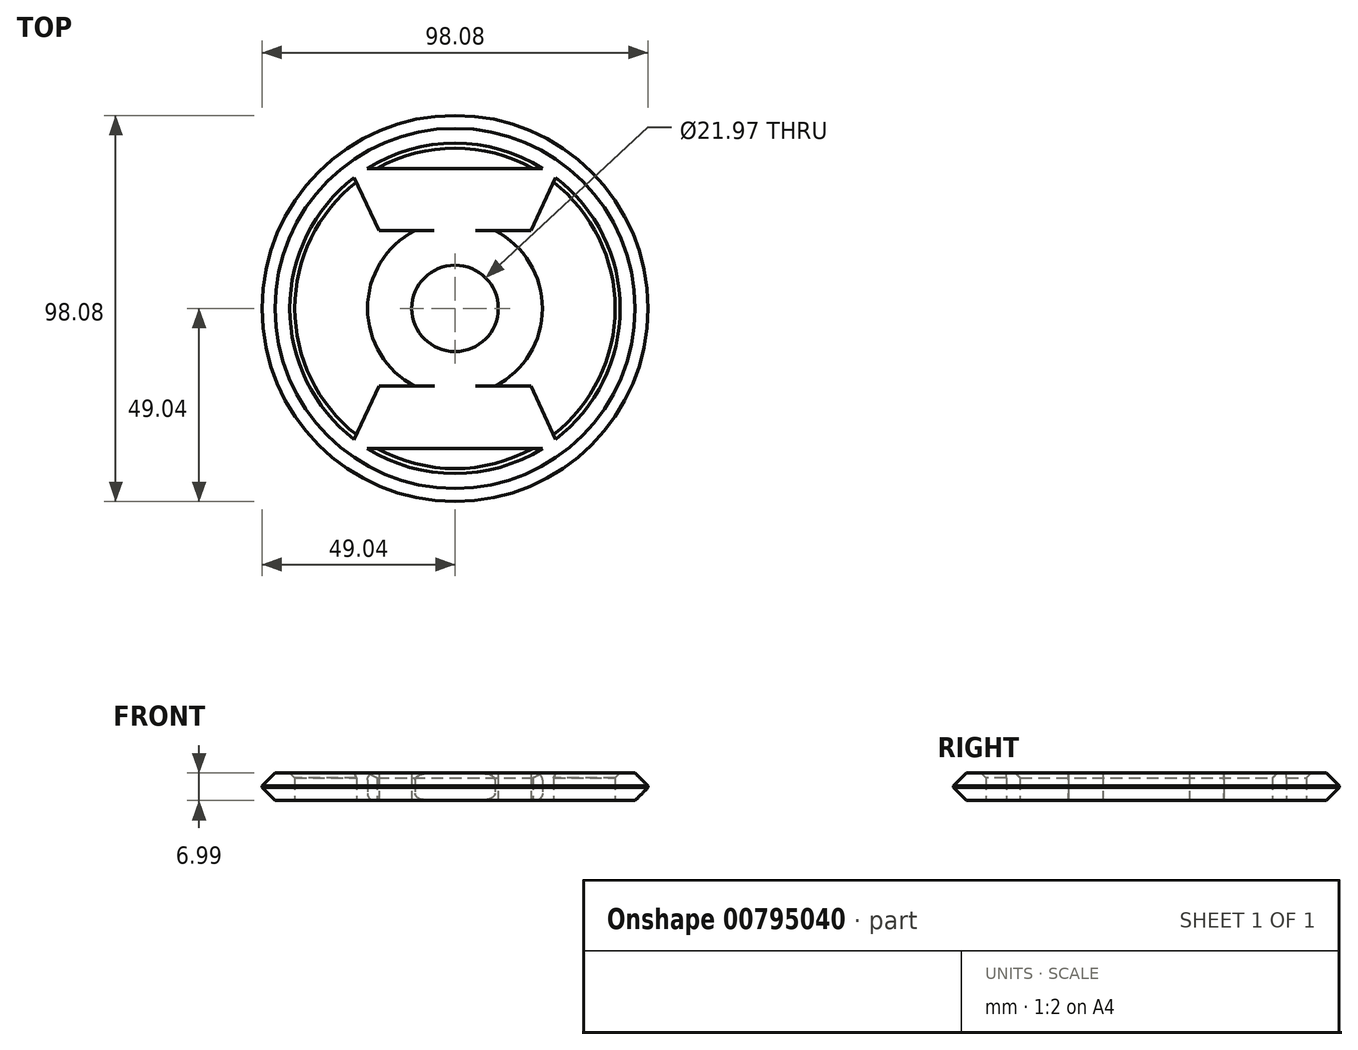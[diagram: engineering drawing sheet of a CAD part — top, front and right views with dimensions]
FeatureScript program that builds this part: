
annotation { "Feature Type Name" : "Feature", "Feature Type Description" : "" }
export const myFeature = defineFeature(function(context is Context, id is Id, definition is map)
    precondition{}
    {
        {
            var Q0;
            Q0=qCreatedBy(makeId("Top.planeOp"),FACE);
            var sketch = newSketch(context, id + "F0", { "sketchPlane" : qUnion([Q0])});
            skCircle(sketch, "E0", {"center": v(0, 0) * mm, "radius": 10.99 * mm});
            skCircle(sketch, "E1", {"center": v(0, 0) * mm, "radius": 22.23 * mm});
            skPoint(sketch, "E2", {"position": v(0, 35.56) * mm});
            skPoint(sketch, "E3", {"position": v(0, -35.56) * mm});
            skPoint(sketch, "E4", {"position": v(-26.67, 35.56) * mm});
            skPoint(sketch, "E5", {"position": v(26.67, 35.56) * mm});
            skPoint(sketch, "E6", {"position": v(-26.67, -35.56) * mm});
            skPoint(sketch, "E7", {"position": v(26.67, -35.56) * mm});
            skLineSegment(sketch, "E8", {"start": v(-26.67, 35.56) * mm, "end": v(26.67, 35.56) * mm});
            skLineSegment(sketch, "E9", {"start": v(-26.67, -35.56) * mm, "end": v(26.67, -35.56) * mm});
            skPoint(sketch, "E10", {"position": v(0, 19.75) * mm});
            skLineSegment(sketch, "E11", {"start": v(-26.67, 35.56) * mm, "end": v(-19.3, 19.75) * mm});
            skLineSegment(sketch, "E12", {"start": v(0, 19.75) * mm, "end": v(-19.3, 19.75) * mm});
            skLineSegment(sketch, "E13", {"start": v(0, 19.75) * mm, "end": v(19.3, 19.75) * mm});
            skLineSegment(sketch, "E14", {"start": v(26.67, 35.56) * mm, "end": v(19.3, 19.75) * mm});
            skPoint(sketch, "E15", {"position": v(0, -19.76) * mm});
            skLineSegment(sketch, "E16", {"start": v(0, -19.76) * mm, "end": v(-19.3, -19.76) * mm});
            skLineSegment(sketch, "E17", {"start": v(-19.3, -19.76) * mm, "end": v(-26.67, -35.56) * mm});
            skLineSegment(sketch, "E18", {"start": v(0, -19.76) * mm, "end": v(19.3, -19.76) * mm});
            skLineSegment(sketch, "E19", {"start": v(19.3, -19.76) * mm, "end": v(26.67, -35.56) * mm});
            skCircle(sketch, "E20", {"center": v(0, 0) * mm, "radius": 40.7 * mm});
            skCircle(sketch, "E21", {"center": v(0, 0) * mm, "radius": 49.04 * mm});
            skSolve(sketch);
        }
        {
            var Q0;
            Q0=makeQuery(id+"F0.imprint","IMPRINT",FACE,{"disambiguationData":[TD([[makeQuery(id+"F0.imprint","IMPRINT",EDGE,{"derivedFrom":sQuery(id+"F0.wireOp",EDGE,"E21")}),1.0]])]});
            var Q1;
            {var subQ0=sQuery(id+"F0.wireOp",EDGE,"E12");var subQ3=sQuery(id+"F0.wireOp",EDGE,"E1");var subQ4=makeQuery(id+"F0.imprint","INTERSECT",VERTEX,{"derivedFrom":[subQ3,subQ0]});Q1=makeQuery(id+"F0.imprint","IMPRINT",FACE,{"disambiguationData":[TD([[makeQuery(id+"F0.imprint","IMPRINT",EDGE,{"disambiguationData":[TD([[subQ4,1.0]])],"derivedFrom":subQ3}),-1.0]])]});}
            var Q2;
            {var subQ0=sQuery(id+"F0.wireOp",EDGE,"E11");var subQ1=sQuery(id+"F0.wireOp",EDGE,"E8");var subQ2=makeQuery(id+"F0.imprint","INTERSECT",VERTEX,{"derivedFrom":[subQ1,subQ0]});Q2=makeQuery(id+"F0.imprint","IMPRINT",FACE,{"disambiguationData":[TD([[makeQuery(id+"F0.imprint","IMPRINT",EDGE,{"disambiguationData":[TD([[subQ2,-1.0]])],"derivedFrom":subQ1}),-1.0]])]});}
            var Q3;
            {var subQ0=sQuery(id+"F0.wireOp",EDGE,"E14");var subQ1=sQuery(id+"F0.wireOp",EDGE,"E8");var subQ2=makeQuery(id+"F0.imprint","INTERSECT",VERTEX,{"derivedFrom":[subQ1,subQ0]});Q3=makeQuery(id+"F0.imprint","IMPRINT",FACE,{"disambiguationData":[TD([[makeQuery(id+"F0.imprint","IMPRINT",EDGE,{"disambiguationData":[TD([[subQ2,1.0]])],"derivedFrom":subQ1}),-1.0]])]});}
            var Q4;
            Q4=makeQuery(id+"F0.imprint","IMPRINT",FACE,{"disambiguationData":[TD([[makeQuery(id+"F0.imprint","IMPRINT",EDGE,{"derivedFrom":sQuery(id+"F0.wireOp",EDGE,"E0")}),-1.0]])]});
            var Q5;
            {var subQ0=sQuery(id+"F0.wireOp",EDGE,"E12");var subQ1=sQuery(id+"F0.wireOp",EDGE,"E1");var subQ2=makeQuery(id+"F0.imprint","INTERSECT",VERTEX,{"derivedFrom":[subQ1,subQ0]});Q5=makeQuery(id+"F0.imprint","IMPRINT",FACE,{"disambiguationData":[TD([[makeQuery(id+"F0.imprint","IMPRINT",EDGE,{"disambiguationData":[TD([[subQ2,1.0]])],"derivedFrom":subQ1}),1.0]])]});}
            var Q6;
            {var subQ1=sQuery(id+"F0.wireOp",EDGE,"E16");var subQ5=sQuery(id+"F0.wireOp",EDGE,"E1");var subQ6=makeQuery(id+"F0.imprint","INTERSECT",VERTEX,{"derivedFrom":[subQ5,subQ1]});Q6=makeQuery(id+"F0.imprint","IMPRINT",FACE,{"disambiguationData":[TD([[makeQuery(id+"F0.imprint","IMPRINT",EDGE,{"disambiguationData":[TD([[subQ6,-1.0]])],"derivedFrom":subQ5}),-1.0]])]});}
            var Q7;
            {var subQ0=sQuery(id+"F0.wireOp",EDGE,"E16");var subQ1=sQuery(id+"F0.wireOp",EDGE,"E1");var subQ2=makeQuery(id+"F0.imprint","INTERSECT",VERTEX,{"derivedFrom":[subQ1,subQ0]});Q7=makeQuery(id+"F0.imprint","IMPRINT",FACE,{"disambiguationData":[TD([[makeQuery(id+"F0.imprint","IMPRINT",EDGE,{"disambiguationData":[TD([[subQ2,-1.0]])],"derivedFrom":subQ1}),1.0]])]});}
            var Q8;
            {var subQ0=sQuery(id+"F0.wireOp",EDGE,"E17");var subQ1=sQuery(id+"F0.wireOp",EDGE,"E9");var subQ2=makeQuery(id+"F0.imprint","INTERSECT",VERTEX,{"derivedFrom":[subQ1,subQ0]});Q8=makeQuery(id+"F0.imprint","IMPRINT",FACE,{"disambiguationData":[TD([[makeQuery(id+"F0.imprint","IMPRINT",EDGE,{"disambiguationData":[TD([[subQ2,-1.0]])],"derivedFrom":subQ1}),1.0]])]});}
            var Q9;
            {var subQ0=sQuery(id+"F0.wireOp",EDGE,"E19");var subQ1=sQuery(id+"F0.wireOp",EDGE,"E9");var subQ2=makeQuery(id+"F0.imprint","INTERSECT",VERTEX,{"derivedFrom":[subQ1,subQ0]});Q9=makeQuery(id+"F0.imprint","IMPRINT",FACE,{"disambiguationData":[TD([[makeQuery(id+"F0.imprint","IMPRINT",EDGE,{"disambiguationData":[TD([[subQ2,1.0]])],"derivedFrom":subQ1}),1.0]])]});}
            extrude(context, id + "F1", {"entities" : qUnion([Q0, Q1, Q2, Q3, Q4, Q5, Q6, Q7, Q8, Q9]), "depth" : 7 * mm, "offsetDistance" : 25.4 * mm});
        }
        {
            var Q0;
            {var subQ0=sQuery(id+"F0.wireOp",EDGE,"E1");Q0=makeQuery(id+"F1.opExtrude","CAP_EDGE",EDGE,{"disambiguationData":[OSD([subQ0]),TDD([makeQuery(id+"F0.imprint","IMPRINT",EDGE,{"disambiguationData":[TD([[makeQuery(id+"F0.imprint","INTERSECT",VERTEX,{"derivedFrom":[subQ0,sQuery(id+"F0.wireOp",EDGE,"E12")]}),-1.0]])],"derivedFrom":subQ0})])],"isStart":false});}
            var Q1;
            {var subQ0=sQuery(id+"F0.wireOp",EDGE,"E1");Q1=makeQuery(id+"F1.opExtrude","CAP_EDGE",EDGE,{"disambiguationData":[OSD([subQ0]),TDD([makeQuery(id+"F0.imprint","IMPRINT",EDGE,{"disambiguationData":[TD([[makeQuery(id+"F0.imprint","INTERSECT",VERTEX,{"derivedFrom":[subQ0,sQuery(id+"F0.wireOp",EDGE,"E13")]}),1.0]])],"derivedFrom":subQ0})])],"isStart":false});}
            var Q2;
            {var subQ0=sQuery(id+"F0.wireOp",EDGE,"E1");Q2=makeQuery(id+"F1.opExtrude","CAP_EDGE",EDGE,{"disambiguationData":[OSD([subQ0]),TDD([makeQuery(id+"F0.imprint","IMPRINT",EDGE,{"disambiguationData":[TD([[makeQuery(id+"F0.imprint","INTERSECT",VERTEX,{"derivedFrom":[subQ0,sQuery(id+"F0.wireOp",EDGE,"E13")]}),1.0]])],"derivedFrom":subQ0})])],"isStart":true});}
            var Q3;
            {var subQ0=sQuery(id+"F0.wireOp",EDGE,"E1");Q3=makeQuery(id+"F1.opExtrude","CAP_EDGE",EDGE,{"disambiguationData":[OSD([subQ0]),TDD([makeQuery(id+"F0.imprint","IMPRINT",EDGE,{"disambiguationData":[TD([[makeQuery(id+"F0.imprint","INTERSECT",VERTEX,{"derivedFrom":[subQ0,sQuery(id+"F0.wireOp",EDGE,"E12")]}),-1.0]])],"derivedFrom":subQ0})])],"isStart":true});}
            fillet(context, id + "F2", {"entities" : qUnion([Q0, Q1, Q2, Q3]), "radius" : 1.78 * mm, "tangentPropagation" : true, "allowEdgeOverflow" : false});
        }
        {
            var Q0;
            {var subQ0=sQuery(id+"F0.wireOp",EDGE,"E20");Q0=makeQuery(id+"F1.opExtrude","CAP_EDGE",EDGE,{"disambiguationData":[OSD([subQ0]),TDD([makeQuery(id+"F0.imprint","IMPRINT",EDGE,{"disambiguationData":[TD([[makeQuery(id+"F0.imprint","INTERSECT",VERTEX,{"derivedFrom":[sQuery(id+"F0.wireOp",EDGE,"E11"),subQ0]}),-1.0]])],"derivedFrom":subQ0})])],"isStart":false});}
            var Q1;
            {var subQ0=sQuery(id+"F0.wireOp",EDGE,"E20");var subQ1=sQuery(id+"F0.wireOp",EDGE,"E8");Q1=makeQuery(id+"F1.opExtrude","CAP_EDGE",EDGE,{"disambiguationData":[OSD([subQ0]),TDD([makeQuery(id+"F0.imprint","IMPRINT",EDGE,{"disambiguationData":[TD([[makeQuery(id+"F0.imprint","INTERSECT",VERTEX,{"disambiguationData":[OD(0.0)],"derivedFrom":[subQ1,subQ0]}),1.0]])],"derivedFrom":subQ0})])],"isStart":false});}
            var Q2;
            {var subQ0=sQuery(id+"F0.wireOp",EDGE,"E20");Q2=makeQuery(id+"F1.opExtrude","CAP_EDGE",EDGE,{"disambiguationData":[OSD([subQ0]),TDD([makeQuery(id+"F0.imprint","IMPRINT",EDGE,{"disambiguationData":[TD([[makeQuery(id+"F0.imprint","INTERSECT",VERTEX,{"derivedFrom":[sQuery(id+"F0.wireOp",EDGE,"E14"),subQ0]}),1.0]])],"derivedFrom":subQ0})])],"isStart":false});}
            var Q3;
            {var subQ0=sQuery(id+"F0.wireOp",EDGE,"E20");var subQ1=sQuery(id+"F0.wireOp",EDGE,"E9");Q3=makeQuery(id+"F1.opExtrude","CAP_EDGE",EDGE,{"disambiguationData":[OSD([subQ0]),TDD([makeQuery(id+"F0.imprint","IMPRINT",EDGE,{"disambiguationData":[TD([[makeQuery(id+"F0.imprint","INTERSECT",VERTEX,{"disambiguationData":[OD(0.0)],"derivedFrom":[subQ1,subQ0]}),-1.0]])],"derivedFrom":subQ0})])],"isStart":false});}
            chamfer(context, id + "F3", {"entities" : qUnion([Q0, Q1, Q2, Q3]), "width" : 1.27 * mm, "tangentPropagation" : true});
        }
        {
            var Q0;
            Q0=makeQuery(id+"F1.opExtrude","CAP_EDGE",EDGE,{"disambiguationData":[OSD([sQuery(id+"F0.wireOp",EDGE,"E21")])],"isStart":false});
            var Q1;
            Q1=makeQuery(id+"F1.opExtrude","CAP_EDGE",EDGE,{"disambiguationData":[OSD([sQuery(id+"F0.wireOp",EDGE,"E21")])],"isStart":true});
            chamfer(context, id + "F4", {"entities" : qUnion([Q0, Q1]), "width" : 3.3 * mm, "tangentPropagation" : true});
        }
    });
